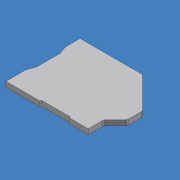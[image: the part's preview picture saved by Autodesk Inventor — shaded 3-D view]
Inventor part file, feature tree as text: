
AUTODESK INVENTOR PART (.ipt)
format: ipt  version: unknown  size: 173,056 bytes
history: native  units: mm (DEFAULTED — no unit token found)
features: extrude x1, sketch x1
ambient origin geometry x8: Origin, YZ Plane, XZ Plane, XY Plane, X Axis, Y Axis, Z Axis, Center Point
feature tree (2):
  extrude  "Extrusion1"  [1 undecoded]
  sketch  "Skizze_1"  dims[d0=1.6mm d1=0.0mm]
note: 1 required parameter value undecoded (feature->parameter linkage not recoverable at this tier; creation-order binding heuristic only, values carry confidence <= 0.55)
